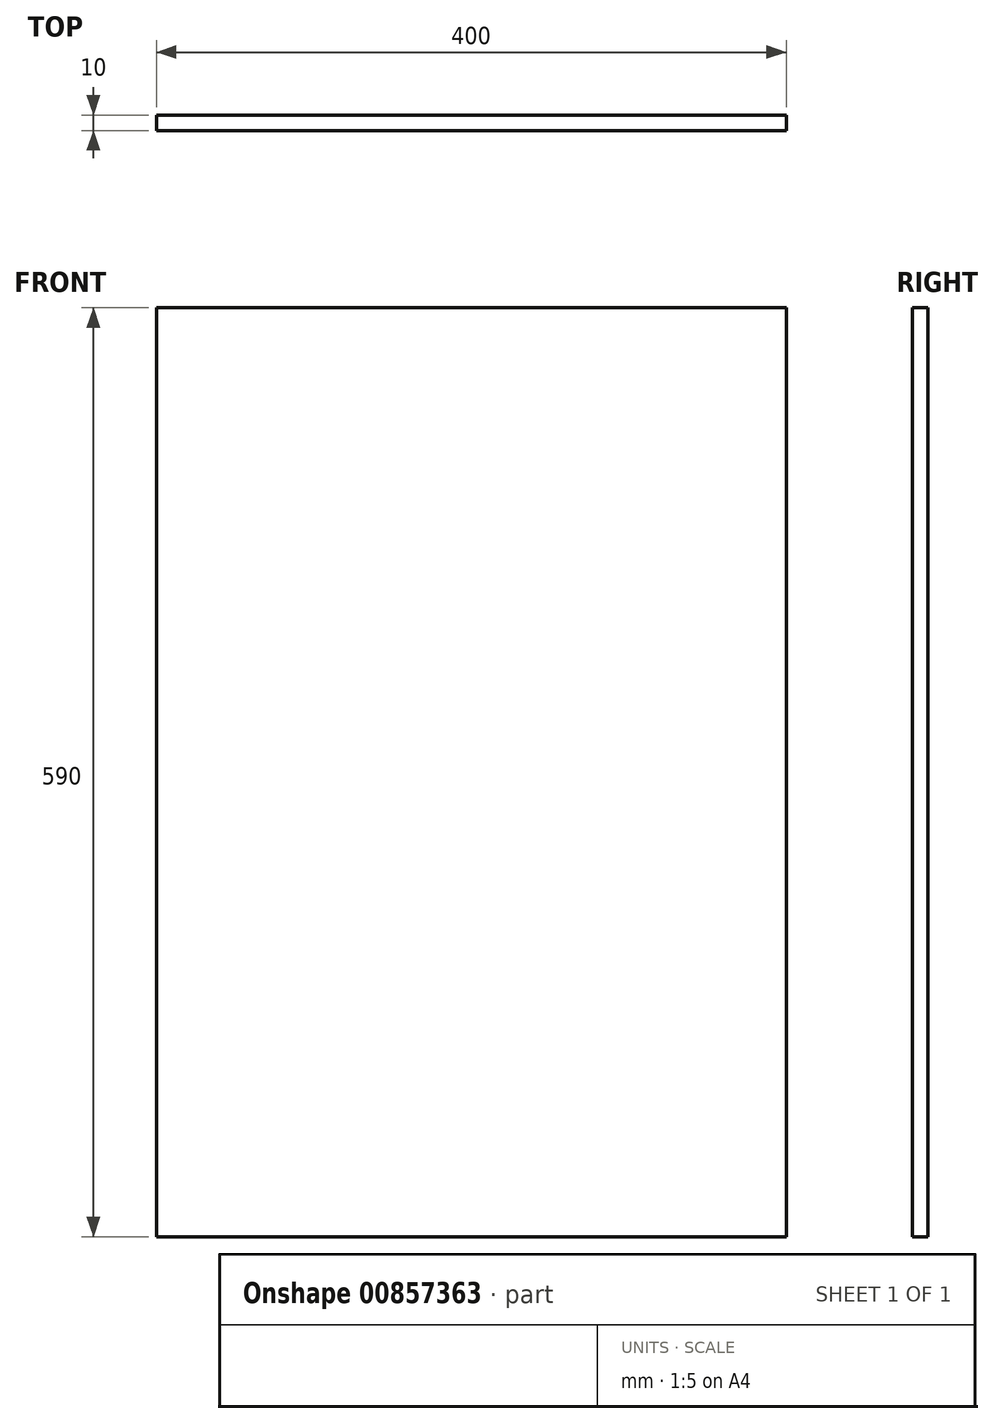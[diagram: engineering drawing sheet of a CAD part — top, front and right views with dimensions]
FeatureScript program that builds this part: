
annotation { "Feature Type Name" : "Feature", "Feature Type Description" : "" }
export const myFeature = defineFeature(function(context is Context, id is Id, definition is map)
    precondition{}
    {
        {
            var Q0;
            Q0=qCreatedBy(makeId("Front.planeOp"),FACE);
            var sketch = newSketch(context, id + "F0", { "sketchPlane" : qUnion([Q0])});
            skLineSegment(sketch, "E0.bottom", {"start": v(-200, 295) * mm, "end": v(200, 295) * mm});
            skLineSegment(sketch, "E0.top", {"start": v(-200, -295) * mm, "end": v(200, -295) * mm});
            skLineSegment(sketch, "E0.left", {"start": v(-200, 295) * mm, "end": v(-200, -295) * mm});
            skLineSegment(sketch, "E0.right", {"start": v(200, 295) * mm, "end": v(200, -295) * mm});
            skSolve(sketch);
        }
        {
            var Q0;
            Q0=makeQuery(id+"F0.imprint","IMPRINT",FACE,{"disambiguationData":[TD([[makeQuery(id+"F0.imprint","IMPRINT",EDGE,{"derivedFrom":sQuery(id+"F0.wireOp",EDGE,"E0.bottom")}),-1.0]])]});
            extrude(context, id + "F1", {"entities" : qUnion([Q0]), "depth" : 10 * mm, "offsetDistance" : 25 * mm});
        }
    });
